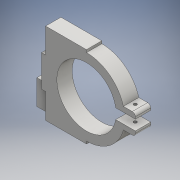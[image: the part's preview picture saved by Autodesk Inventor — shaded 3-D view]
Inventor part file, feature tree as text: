
AUTODESK INVENTOR PART (.ipt)
format: ipt  version: 2016 (Build 200138000, 138)  size: 177,664 bytes
history: native  units: mm
features: sketch x8, extrude x6, hole x2, fillet x1
ambient origin geometry x8: Origin, YZ Plane, XZ Plane, XY Plane, X Axis, Y Axis, Z Axis, Center Point
bodies: Solid1 (feature_tree)
feature tree (17):
  extrude  "Extrusion1"  Depth=80.0mm
  hole  "Hole1"  [1 undecoded]
  extrude  "Extrusion2"  Depth=10.0mm
  extrude  "Extrusion3"  Depth=15.0mm
  extrude  "Extrusion4"  Depth=15.0mm TaperAngle=0.0deg
  fillet  "Fillet1"  Radius=3.0mm
  hole  "Hole2"  [1 undecoded]
  extrude  "Extrusion5"  Depth=24.5mm
  extrude  "Extrusion6"  Depth=4.0mm TaperAngle=0.0deg
  sketch  "Sketch1"  dims[d0=80.0mm d1=80.0mm]
  sketch  "Sketch2"  dims[d2=15.0mm d3=0.0mm]
  sketch  "Sketch3"  dims[d4=58.0mm d5=6.0mm d6=4.0mm d7=2.0mm d8=90.0deg d9=8.0mm d10=20.594885mm d11=75.0mm]
  sketch  "Sketch4"  dims[d12=15.0mm d13=0.0mm d14=10.0mm]
  sketch  "Sketch5"  dims[d15=15.0mm d16=0.0mm d17=15.0mm]
  sketch  "Sketch6"  dims[d18=5.0mm d19=15.0mm d20=0.0mm d21=3.0mm]
  sketch  "Sketch7"  dims[d22=4.6155mm]
  sketch  "Sketch8"  dims[d23=3.0mm d24=6.0mm d25=4.0mm d26=2.0mm d27=90.0deg d28=8.0mm d29=20.594885mm d30=31.0mm d31=24.5mm d32=4.0mm d33=0.0mm d34=7.5mm d35=16.0mm d36=0.0mm]
note: 2 required parameter values undecoded (feature->parameter linkage not recoverable at this tier; creation-order binding heuristic only, values carry confidence <= 0.55)
